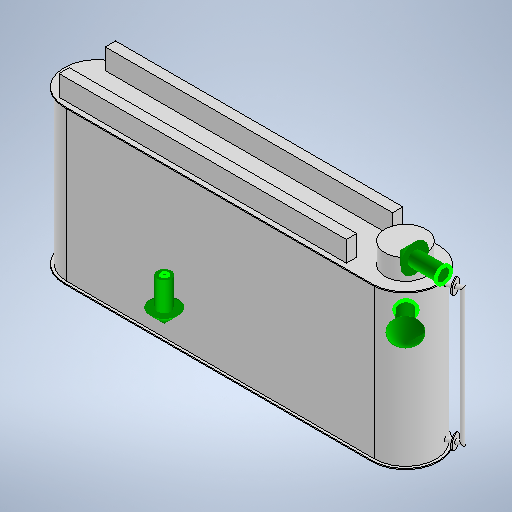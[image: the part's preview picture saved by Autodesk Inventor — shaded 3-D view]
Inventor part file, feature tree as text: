
AUTODESK INVENTOR PART (.ipt)
format: ipt  version: 2025 (Build 290162010, 162A)  size: 331,264 bytes
history: native  units: mm
features: sketch x12, other x3, plane x3
ambient origin geometry x8: Origin, YZ Plane, XZ Plane, XY Plane, X Axis, Y Axis, Z Axis, Center Point
bodies: Solid1 (feature_tree)
feature tree (18):
  other  "GNG НаOCl tank 2.ipt"
  other  "Solid1::GNG НаOCl tank 2.ipt"
  other  "TaggingFeature1"
  sketch  "Sketch1"  dims[d0=10.0mm]
  sketch  "Sketch2"
  sketch  "Sketch3"
  sketch  "Sketch4"
  sketch  "Sketch5"
  sketch  "Sketch6"
  sketch  "Sketch7"
  sketch  "Sketch8"
  sketch  "Sketch9"
  sketch  "Sketch10"
  sketch  "Sketch15"
  sketch  "Sketch16"
  plane  "Work Plane1"
  plane  "Work Plane2"
  plane  "Work Plane3"
